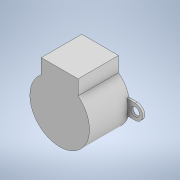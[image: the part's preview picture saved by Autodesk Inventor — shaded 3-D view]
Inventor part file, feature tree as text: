
AUTODESK INVENTOR PART (.ipt)
format: ipt  version: 2021 (Build 250183000, 183)  size: 151,040 bytes
history: native  units: mm
features: extrude x5, sketch x5, projected_geometry x2, mirror x1
ambient origin geometry x8: Origin, YZ Plane, XZ Plane, XY Plane, X Axis, Y Axis, Z Axis, Center Point
bodies: Solid1 (feature_tree)
feature tree (13):
  extrude  "Extrusion1"  Depth=19.0mm TaperAngle=0.0deg
  extrude  "Extrusion2"  Depth=17.3mm
  extrude  "Extrusion3"  Depth=19.0mm
  mirror  "Mirror1"
  extrude  "Extrusion4"  Depth=7.0mm
  extrude  "Extrusion5"  Depth=9.5mm
  sketch  "Sketch1"  dims[d0=28.0mm d1=19.0mm d2=0.0mm]
  sketch  "Sketch2"  dims[d3=17.3mm d4=32.0mm]
  sketch  "Sketch3"  dims[d5=19.0mm d6=0.0mm d7=21.0mm]
  sketch  "Sketch4"  dims[d8=7.0mm d9=4.0mm]
  sketch  "Sketch5"  dims[d10=1.0mm d11=0.0mm d12=9.5mm d13=20.5mm d14=1.5mm d15=0.0mm d16=5.0mm d17=8.0mm d18=0.0mm]
  projected_geometry  "Project Cut Edges1"
  projected_geometry  "Project Cut Edges2"
